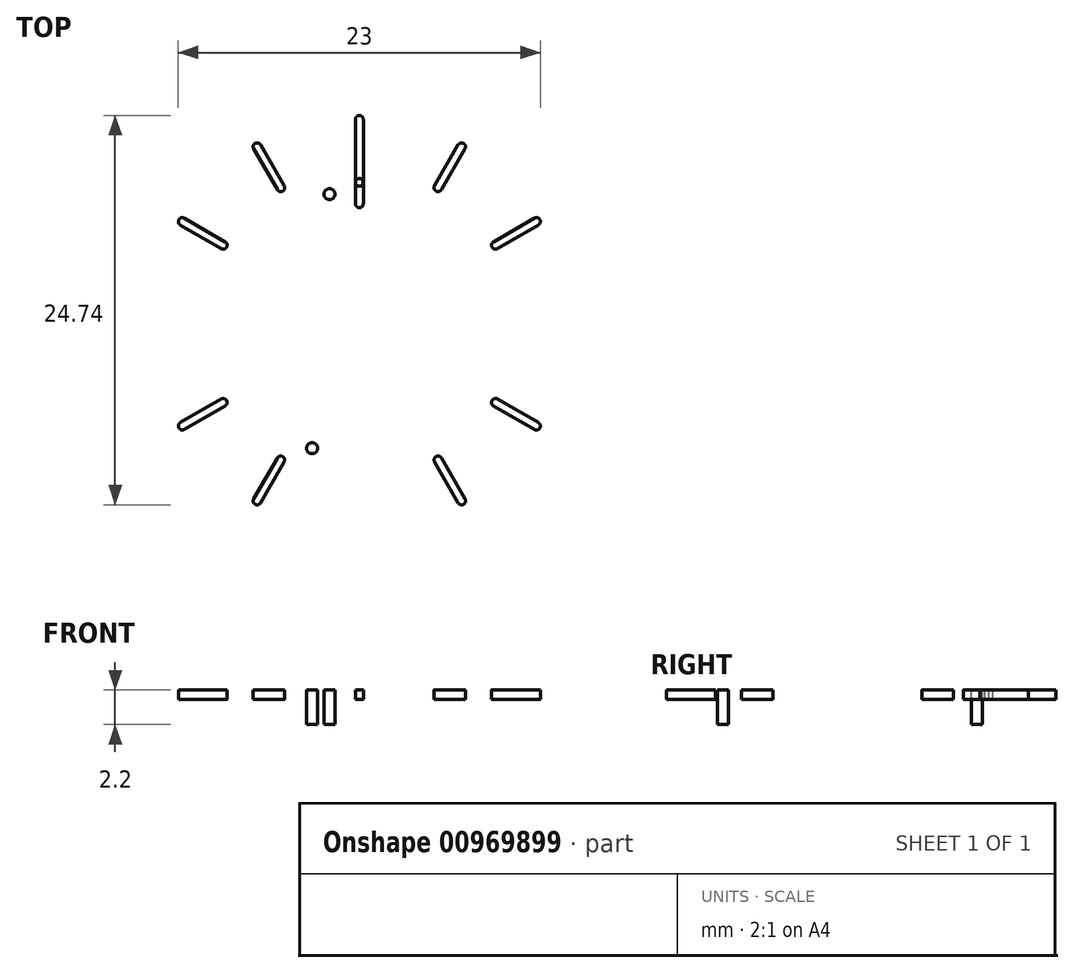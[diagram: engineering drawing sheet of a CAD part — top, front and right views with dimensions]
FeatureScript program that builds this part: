
annotation { "Feature Type Name" : "Feature", "Feature Type Description" : "" }
export const myFeature = defineFeature(function(context is Context, id is Id, definition is map)
    precondition{}
    {
        {
            var Q0;
            Q0=qCreatedBy(makeId("Top.planeOp"),FACE);
            var sketch = newSketch(context, id + "F0", { "sketchPlane" : qUnion([Q0])});
            skCircle(sketch, "E0", {"center": v(0, 0) * mm, "radius": 13.38 * mm});
            skLineSegment(sketch, "E1", {"start": v(0, -5.55) * mm, "end": v(0, 0) * mm, "construction": true});
            skLineSegment(sketch, "E2", {"start": v(-1.74, -5.55) * mm, "end": v(-4.94, -5.55) * mm, "construction": true});
            skLineSegment(sketch, "E3", {"start": v(0, -5.55) * mm, "end": v(3.2, -5.55) * mm, "construction": true});
            skLineSegment(sketch, "E4", {"start": v(-2.74, -5.55) * mm, "end": v(-2.74, -3.05) * mm, "construction": true});
            skLineSegment(sketch, "E5", {"start": v(3.2, -3.05) * mm, "end": v(3.2, -5.55) * mm, "construction": true});
            skLineSegment(sketch, "E6", {"start": v(-4.94, -3.15) * mm, "end": v(-2.81, -3.15) * mm, "construction": true});
            skLineSegment(sketch, "E7", {"start": v(-2.35, -3.15) * mm, "end": v(-2.35, -5.55) * mm, "construction": true});
            skLineSegment(sketch, "E8", {"start": v(-2.35, -5.55) * mm, "end": v(-0.22, -5.55) * mm, "construction": true});
            skArc(sketch, "E9.0.startCap", {"start": v(-3.03, -5.43) * mm, "mid": v(-3.22, -5.52) * mm, "end": v(-3.32, -5.33) * mm});
            skArc(sketch, "E9.0.endCap", {"start": v(-2.6, -3.14) * mm, "mid": v(-2.47, -3.04) * mm, "end": v(-2.33, -3.13) * mm});
            skLineSegment(sketch, "E9.0.left", {"start": v(-3.32, -5.33) * mm, "end": v(-2.6, -3.14) * mm});
            skLineSegment(sketch, "E9.0.right", {"start": v(-3.03, -5.43) * mm, "end": v(-2.46, -3.64) * mm});
            skArc(sketch, "E9.1.startCap", {"start": v(-2.6, -3.14) * mm, "mid": v(-2.47, -3.04) * mm, "end": v(-2.33, -3.13) * mm});
            skArc(sketch, "E9.1.endCap", {"start": v(-1.5, -5.33) * mm, "mid": v(-1.59, -5.52) * mm, "end": v(-1.78, -5.43) * mm});
            skLineSegment(sketch, "E9.1.left", {"start": v(-2.33, -3.13) * mm, "end": v(-1.5, -5.33) * mm});
            skLineSegment(sketch, "E9.1.right", {"start": v(-2.46, -3.64) * mm, "end": v(-1.78, -5.43) * mm});
            skLineSegment(sketch, "E10", {"start": v(-0.59, -3.05) * mm, "end": v(-0.59, -5.55) * mm, "construction": true});
            skArc(sketch, "E11.0.startCap", {"start": v(-1.5, -5.41) * mm, "mid": v(-1.68, -5.51) * mm, "end": v(-1.78, -5.33) * mm});
            skArc(sketch, "E11.0.endCap", {"start": v(-1.14, -3.16) * mm, "mid": v(-1, -3.05) * mm, "end": v(-0.86, -3.15) * mm});
            skLineSegment(sketch, "E11.0.left", {"start": v(-1.78, -5.33) * mm, "end": v(-1.14, -3.16) * mm});
            skLineSegment(sketch, "E11.0.right", {"start": v(-1.5, -5.41) * mm, "end": v(-0.97, -3.66) * mm});
            skArc(sketch, "E11.1.startCap", {"start": v(-1.14, -3.16) * mm, "mid": v(-1, -3.05) * mm, "end": v(-0.86, -3.15) * mm});
            skArc(sketch, "E11.1.endCap", {"start": v(0.02, -5.31) * mm, "mid": v(-0.06, -5.5) * mm, "end": v(-0.26, -5.43) * mm});
            skLineSegment(sketch, "E11.1.left", {"start": v(-0.86, -3.15) * mm, "end": v(0.02, -5.31) * mm});
            skLineSegment(sketch, "E11.1.right", {"start": v(-0.97, -3.66) * mm, "end": v(-0.26, -5.43) * mm});
            skLineSegment(sketch, "E12", {"start": v(1.33, -5.36) * mm, "end": v(1.33, -4.43) * mm});
            skLineSegment(sketch, "E13", {"start": v(1.33, -5.36) * mm, "end": v(1.63, -5.36) * mm});
            skLineSegment(sketch, "E14", {"start": v(1.63, -5.36) * mm, "end": v(1.63, -4.43) * mm});
            skLineSegment(sketch, "E15", {"start": v(1.63, -4.43) * mm, "end": v(2.48, -4.07) * mm});
            skLineSegment(sketch, "E16", {"start": v(1.33, -4.43) * mm, "end": v(1.33, -4.25) * mm});
            skLineSegment(sketch, "E17", {"start": v(1.33, -4.25) * mm, "end": v(2.36, -3.8) * mm});
            skLineSegment(sketch, "E18", {"start": v(2.36, -3.8) * mm, "end": v(1.33, -3.37) * mm});
            skLineSegment(sketch, "E19", {"start": v(1.63, -3.15) * mm, "end": v(2.61, -3.56) * mm});
            skLineSegment(sketch, "E20", {"start": v(2.48, -4.07) * mm, "end": v(2.61, -4.01) * mm});
            skArc(sketch, "E21", {"start": v(1.33, -5.36) * mm, "mid": v(1.48, -5.51) * mm, "end": v(1.63, -5.36) * mm});
            skArc(sketch, "E22", {"start": v(1.45, -3.07) * mm, "mid": v(1.3, -3.19) * mm, "end": v(1.33, -3.37) * mm});
            skArc(sketch, "E23", {"start": v(2.61, -4.01) * mm, "mid": v(2.72, -3.79) * mm, "end": v(2.61, -3.56) * mm});
            skPoint(sketch, "E24.orphan", {"position": v(2.48, -3.5) * mm});
            skLineSegment(sketch, "E25", {"start": v(1.63, -3.15) * mm, "end": v(1.45, -3.07) * mm});
            skPoint(sketch, "E26.end.orphan", {"position": v(1.33, -3.15) * mm});
            skSolve(sketch);
        }
        {
            var Q0;
            Q0=makeQuery(id+"F0.imprint","IMPRINT",FACE,{"disambiguationData":[TD([[makeQuery(id+"F0.imprint","IMPRINT",EDGE,{"derivedFrom":sQuery(id+"F0.wireOp",EDGE,"E0")}),1.0]])]});
            extrude(context, id + "F1", {"entities" : qUnion([Q0]), "depth" : .6 * mm});
        }
        {
            var Q0;
            Q0=makeQuery(id+"F1.opExtrude","CAP_FACE",FACE,{"disambiguationData":[OSD([sQuery(id+"F0.wireOp",EDGE,"E0"),sQuery(id+"F0.wireOp",EDGE,"81bd0466-aa7e-4cc1-a586-6c7cb0b4c62f.0.endCap"),sQuery(id+"F0.wireOp",EDGE,"81bd0466-aa7e-4cc1-a586-6c7cb0b4c62f.0.left"),sQuery(id+"F0.wireOp",EDGE,"81bd0466-aa7e-4cc1-a586-6c7cb0b4c62f.0.right"),sQuery(id+"F0.wireOp",EDGE,"81bd0466-aa7e-4cc1-a586-6c7cb0b4c62f.1.startCap"),sQuery(id+"F0.wireOp",EDGE,"81bd0466-aa7e-4cc1-a586-6c7cb0b4c62f.1.endCap"),sQuery(id+"F0.wireOp",EDGE,"81bd0466-aa7e-4cc1-a586-6c7cb0b4c62f.1.left"),sQuery(id+"F0.wireOp",EDGE,"81bd0466-aa7e-4cc1-a586-6c7cb0b4c62f.1.right"),sQuery(id+"F0.wireOp",EDGE,"fb5c5668-780e-4590-b6ff-0544ae9edb93.0.startCap"),sQuery(id+"F0.wireOp",EDGE,"fb5c5668-780e-4590-b6ff-0544ae9edb93.0.left"),sQuery(id+"F0.wireOp",EDGE,"fb5c5668-780e-4590-b6ff-0544ae9edb93.0.right"),sQuery(id+"F0.wireOp",EDGE,"fb5c5668-780e-4590-b6ff-0544ae9edb93.1.startCap"),sQuery(id+"F0.wireOp",EDGE,"fb5c5668-780e-4590-b6ff-0544ae9edb93.1.endCap"),sQuery(id+"F0.wireOp",EDGE,"fb5c5668-780e-4590-b6ff-0544ae9edb93.1.left"),sQuery(id+"F0.wireOp",EDGE,"fb5c5668-780e-4590-b6ff-0544ae9edb93.1.right"),sQuery(id+"F0.wireOp",EDGE,"44c2ab98-86a5-4347-a2b7-3f4ff268cd36.0.startCap"),sQuery(id+"F0.wireOp",EDGE,"44c2ab98-86a5-4347-a2b7-3f4ff268cd36.0.left"),sQuery(id+"F0.wireOp",EDGE,"44c2ab98-86a5-4347-a2b7-3f4ff268cd36.0.right"),sQuery(id+"F0.wireOp",EDGE,"44c2ab98-86a5-4347-a2b7-3f4ff268cd36.1.startCap"),sQuery(id+"F0.wireOp",EDGE,"44c2ab98-86a5-4347-a2b7-3f4ff268cd36.1.right"),sQuery(id+"F0.wireOp",EDGE,"44c2ab98-86a5-4347-a2b7-3f4ff268cd36.2.startCap"),sQuery(id+"F0.wireOp",EDGE,"44c2ab98-86a5-4347-a2b7-3f4ff268cd36.2.endCap"),sQuery(id+"F0.wireOp",EDGE,"44c2ab98-86a5-4347-a2b7-3f4ff268cd36.2.left"),sQuery(id+"F0.wireOp",EDGE,"d18c6785-b516-4534-9f84-c989dde87bb4.trimOffspring"),sQuery(id+"F0.wireOp",EDGE,"1f60e2fe-ff87-446b-ac51-922b63681436.trimOffspring")])],"isStart":false});
            var sketch = newSketch(context, id + "F2", { "sketchPlane" : qUnion([Q0])});
            skLineSegment(sketch, "E27", {"start": v(0, 12.99) * mm, "end": v(0, 8.99) * mm});
            skArc(sketch, "E28.0.startCap", {"start": v(-0.25, 12.99) * mm, "mid": v(0, 13.24) * mm, "end": v(0.25, 12.99) * mm});
            skArc(sketch, "E28.0.endCap", {"start": v(0.25, 8.99) * mm, "mid": v(0, 8.74) * mm, "end": v(-0.25, 8.99) * mm});
            skLineSegment(sketch, "E28.0.left", {"start": v(0.25, 12.99) * mm, "end": v(0.25, 8.99) * mm});
            skLineSegment(sketch, "E28.0.right", {"start": v(-0.25, 12.99) * mm, "end": v(-0.25, 8.99) * mm});
            skLineSegment(sketch, "E29.1.0", {"start": v(-12.99, 0.25) * mm, "end": v(-8.99, 0.25) * mm});
            skLineSegment(sketch, "E29.1.1", {"start": v(-12.99, -0.25) * mm, "end": v(-8.99, -0.25) * mm});
            skArc(sketch, "E29.1.2", {"start": v(-12.99, -0.25) * mm, "mid": v(-13.24, 0) * mm, "end": v(-12.99, 0.25) * mm});
            skArc(sketch, "E29.1.3", {"start": v(-8.99, 0.25) * mm, "mid": v(-8.74, 0) * mm, "end": v(-8.99, -0.25) * mm});
            skLineSegment(sketch, "E29.2.0", {"start": v(-0.25, -12.99) * mm, "end": v(-0.25, -8.99) * mm});
            skLineSegment(sketch, "E29.2.1", {"start": v(0.25, -12.99) * mm, "end": v(0.25, -8.99) * mm});
            skArc(sketch, "E29.2.2", {"start": v(0.25, -12.99) * mm, "mid": v(0, -13.24) * mm, "end": v(-0.25, -12.99) * mm});
            skArc(sketch, "E29.2.3", {"start": v(-0.25, -8.99) * mm, "mid": v(0, -8.74) * mm, "end": v(0.25, -8.99) * mm});
            skLineSegment(sketch, "E29.3.0", {"start": v(12.99, -0.25) * mm, "end": v(8.99, -0.25) * mm});
            skLineSegment(sketch, "E29.3.1", {"start": v(12.99, 0.25) * mm, "end": v(8.99, 0.25) * mm});
            skArc(sketch, "E29.3.2", {"start": v(12.99, 0.25) * mm, "mid": v(13.24, 0) * mm, "end": v(12.99, -0.25) * mm});
            skArc(sketch, "E29.3.3", {"start": v(8.99, -0.25) * mm, "mid": v(8.74, 0) * mm, "end": v(8.99, 0.25) * mm});
            skPoint(sketch, "E29.center", {"position": v(0, 0) * mm});
            skLineSegment(sketch, "E30.1.0", {"start": v(6.5, -11.25) * mm, "end": v(5, -8.65) * mm});
            skLineSegment(sketch, "E30.2.0", {"start": v(11.25, -6.5) * mm, "end": v(8.65, -5) * mm});
            skLineSegment(sketch, "E30.4.0", {"start": v(11.25, 6.5) * mm, "end": v(8.65, 5) * mm});
            skLineSegment(sketch, "E30.5.0", {"start": v(6.5, 11.25) * mm, "end": v(5, 8.65) * mm});
            skLineSegment(sketch, "E30.7.0", {"start": v(-6.5, 11.25) * mm, "end": v(-5, 8.65) * mm});
            skLineSegment(sketch, "E30.8.0", {"start": v(-11.25, 6.5) * mm, "end": v(-8.65, 5) * mm});
            skLineSegment(sketch, "E30.10.0", {"start": v(-11.25, -6.5) * mm, "end": v(-8.65, -5) * mm});
            skLineSegment(sketch, "E30.11.0", {"start": v(-6.5, -11.25) * mm, "end": v(-5, -8.65) * mm});
            skArc(sketch, "E31.0.startCap", {"start": v(-11.37, 6.28) * mm, "mid": v(-11.46, 6.62) * mm, "end": v(-11.12, 6.7) * mm});
            skArc(sketch, "E31.0.endCap", {"start": v(-8.52, 5.2) * mm, "mid": v(-8.43, 4.87) * mm, "end": v(-8.77, 4.78) * mm});
            skLineSegment(sketch, "E31.0.left", {"start": v(-11.12, 6.7) * mm, "end": v(-8.52, 5.2) * mm});
            skLineSegment(sketch, "E31.0.right", {"start": v(-11.37, 6.28) * mm, "end": v(-8.77, 4.78) * mm});
            skArc(sketch, "E31.1.startCap", {"start": v(-6.7, 11.12) * mm, "mid": v(-6.62, 11.46) * mm, "end": v(-6.28, 11.37) * mm});
            skArc(sketch, "E31.1.endCap", {"start": v(-4.78, 8.77) * mm, "mid": v(-4.87, 8.43) * mm, "end": v(-5.2, 8.52) * mm});
            skLineSegment(sketch, "E31.1.left", {"start": v(-6.28, 11.37) * mm, "end": v(-4.78, 8.77) * mm});
            skLineSegment(sketch, "E31.1.right", {"start": v(-6.7, 11.12) * mm, "end": v(-5.2, 8.52) * mm});
            skArc(sketch, "E31.2.startCap", {"start": v(6.28, 11.37) * mm, "mid": v(6.62, 11.46) * mm, "end": v(6.7, 11.12) * mm});
            skArc(sketch, "E31.2.endCap", {"start": v(5.2, 8.52) * mm, "mid": v(4.87, 8.43) * mm, "end": v(4.78, 8.77) * mm});
            skLineSegment(sketch, "E31.2.left", {"start": v(6.7, 11.12) * mm, "end": v(5.2, 8.52) * mm});
            skLineSegment(sketch, "E31.2.right", {"start": v(6.28, 11.37) * mm, "end": v(4.78, 8.77) * mm});
            skArc(sketch, "E31.3.startCap", {"start": v(11.12, 6.7) * mm, "mid": v(11.46, 6.62) * mm, "end": v(11.37, 6.28) * mm});
            skArc(sketch, "E31.3.endCap", {"start": v(8.77, 4.78) * mm, "mid": v(8.43, 4.87) * mm, "end": v(8.52, 5.2) * mm});
            skLineSegment(sketch, "E31.3.left", {"start": v(11.37, 6.28) * mm, "end": v(8.77, 4.78) * mm});
            skLineSegment(sketch, "E31.3.right", {"start": v(11.12, 6.7) * mm, "end": v(8.52, 5.2) * mm});
            skArc(sketch, "E31.4.startCap", {"start": v(11.37, -6.28) * mm, "mid": v(11.46, -6.62) * mm, "end": v(11.12, -6.7) * mm});
            skArc(sketch, "E31.4.endCap", {"start": v(8.52, -5.2) * mm, "mid": v(8.43, -4.87) * mm, "end": v(8.77, -4.78) * mm});
            skLineSegment(sketch, "E31.4.left", {"start": v(11.12, -6.7) * mm, "end": v(8.52, -5.2) * mm});
            skLineSegment(sketch, "E31.4.right", {"start": v(11.37, -6.28) * mm, "end": v(8.77, -4.78) * mm});
            skArc(sketch, "E31.5.startCap", {"start": v(6.7, -11.12) * mm, "mid": v(6.62, -11.46) * mm, "end": v(6.28, -11.37) * mm});
            skArc(sketch, "E31.5.endCap", {"start": v(4.78, -8.77) * mm, "mid": v(4.87, -8.43) * mm, "end": v(5.2, -8.52) * mm});
            skLineSegment(sketch, "E31.5.left", {"start": v(6.28, -11.37) * mm, "end": v(4.78, -8.77) * mm});
            skLineSegment(sketch, "E31.5.right", {"start": v(6.7, -11.12) * mm, "end": v(5.2, -8.52) * mm});
            skArc(sketch, "E31.6.startCap", {"start": v(-6.28, -11.37) * mm, "mid": v(-6.62, -11.46) * mm, "end": v(-6.7, -11.12) * mm});
            skArc(sketch, "E31.6.endCap", {"start": v(-5.2, -8.52) * mm, "mid": v(-4.87, -8.43) * mm, "end": v(-4.78, -8.77) * mm});
            skLineSegment(sketch, "E31.6.left", {"start": v(-6.7, -11.12) * mm, "end": v(-5.2, -8.52) * mm});
            skLineSegment(sketch, "E31.6.right", {"start": v(-6.28, -11.37) * mm, "end": v(-4.78, -8.77) * mm});
            skArc(sketch, "E31.7.startCap", {"start": v(-11.12, -6.7) * mm, "mid": v(-11.46, -6.62) * mm, "end": v(-11.37, -6.28) * mm});
            skArc(sketch, "E31.7.endCap", {"start": v(-8.77, -4.78) * mm, "mid": v(-8.43, -4.87) * mm, "end": v(-8.52, -5.2) * mm});
            skLineSegment(sketch, "E31.7.left", {"start": v(-11.37, -6.28) * mm, "end": v(-8.77, -4.78) * mm});
            skLineSegment(sketch, "E31.7.right", {"start": v(-11.12, -6.7) * mm, "end": v(-8.52, -5.2) * mm});
            skCircle(sketch, "E32", {"center": v(0, 0) * mm, "radius": 0.75 * mm});
            skLineSegment(sketch, "E33", {"start": v(0, 8.99) * mm, "end": v(0, 7.63) * mm});
            skPoint(sketch, "E33.endSnap0", {"position": v(0, 8.74) * mm});
            skArc(sketch, "E34.0.startCap", {"start": v(-0.25, 8.99) * mm, "mid": v(0, 9.24) * mm, "end": v(0.25, 8.99) * mm});
            skArc(sketch, "E34.0.endCap", {"start": v(0.25, 7.63) * mm, "mid": v(0, 7.38) * mm, "end": v(-0.25, 7.63) * mm});
            skLineSegment(sketch, "E34.0.left", {"start": v(0.25, 8.99) * mm, "end": v(0.25, 7.63) * mm});
            skLineSegment(sketch, "E34.0.right", {"start": v(-0.25, 8.99) * mm, "end": v(-0.25, 7.63) * mm});
            skSolve(sketch);
        }
        {
            var Q0;
            Q0=makeQuery(id+"F2.imprint","IMPRINT",FACE,{"disambiguationData":[TD([[makeQuery(id+"F2.imprint","IMPRINT",EDGE,{"derivedFrom":sQuery(id+"F2.wireOp",EDGE,"E31.0.startCap")}),-1.0]])]});
            var Q1;
            Q1=makeQuery(id+"F2.imprint","IMPRINT",FACE,{"disambiguationData":[TD([[makeQuery(id+"F2.imprint","IMPRINT",EDGE,{"derivedFrom":sQuery(id+"F2.wireOp",EDGE,"E29.1.0")}),-1.0]])]});
            var Q2;
            Q2=makeQuery(id+"F2.imprint","IMPRINT",FACE,{"disambiguationData":[TD([[makeQuery(id+"F2.imprint","IMPRINT",EDGE,{"derivedFrom":sQuery(id+"F2.wireOp",EDGE,"E31.1.startCap")}),-1.0]])]});
            var Q3;
            Q3=makeQuery(id+"F2.imprint","IMPRINT",FACE,{"disambiguationData":[TD([[makeQuery(id+"F2.imprint","IMPRINT",EDGE,{"derivedFrom":sQuery(id+"F2.wireOp",EDGE,"E28.0.startCap")}),-1.0]])]});
            var Q4;
            Q4=makeQuery(id+"F2.imprint","IMPRINT",FACE,{"disambiguationData":[TD([[makeQuery(id+"F2.imprint","IMPRINT",EDGE,{"derivedFrom":sQuery(id+"F2.wireOp",EDGE,"E31.2.startCap")}),-1.0]])]});
            var Q5;
            Q5=makeQuery(id+"F2.imprint","IMPRINT",FACE,{"disambiguationData":[TD([[makeQuery(id+"F2.imprint","IMPRINT",EDGE,{"derivedFrom":sQuery(id+"F2.wireOp",EDGE,"E31.3.startCap")}),-1.0]])]});
            var Q6;
            Q6=makeQuery(id+"F2.imprint","IMPRINT",FACE,{"disambiguationData":[TD([[makeQuery(id+"F2.imprint","IMPRINT",EDGE,{"derivedFrom":sQuery(id+"F2.wireOp",EDGE,"E29.3.0")}),-1.0]])]});
            var Q7;
            Q7=makeQuery(id+"F2.imprint","IMPRINT",FACE,{"disambiguationData":[TD([[makeQuery(id+"F2.imprint","IMPRINT",EDGE,{"derivedFrom":sQuery(id+"F2.wireOp",EDGE,"E31.4.startCap")}),-1.0]])]});
            var Q8;
            Q8=makeQuery(id+"F2.imprint","IMPRINT",FACE,{"disambiguationData":[TD([[makeQuery(id+"F2.imprint","IMPRINT",EDGE,{"derivedFrom":sQuery(id+"F2.wireOp",EDGE,"E29.2.0")}),-1.0]])]});
            var Q9;
            Q9=makeQuery(id+"F2.imprint","IMPRINT",FACE,{"disambiguationData":[TD([[makeQuery(id+"F2.imprint","IMPRINT",EDGE,{"derivedFrom":sQuery(id+"F2.wireOp",EDGE,"E31.5.startCap")}),-1.0]])]});
            var Q10;
            Q10=makeQuery(id+"F2.imprint","IMPRINT",FACE,{"disambiguationData":[TD([[makeQuery(id+"F2.imprint","IMPRINT",EDGE,{"derivedFrom":sQuery(id+"F2.wireOp",EDGE,"E31.6.startCap")}),-1.0]])]});
            var Q11;
            Q11=makeQuery(id+"F2.imprint","IMPRINT",FACE,{"disambiguationData":[TD([[makeQuery(id+"F2.imprint","IMPRINT",EDGE,{"derivedFrom":sQuery(id+"F2.wireOp",EDGE,"E31.7.startCap")}),-1.0]])]});
            var Q12;
            Q12=makeQuery(id+"F2.imprint","IMPRINT",FACE,{"disambiguationData":[TD([[makeQuery(id+"F2.imprint","IMPRINT",EDGE,{"derivedFrom":sQuery(id+"F2.wireOp",EDGE,"E32")}),1.0]])]});
            var Q13;
            Q13=makeQuery(id+"F2.imprint","IMPRINT",FACE,{"disambiguationData":[TD([[makeQuery(id+"F2.imprint","IMPRINT",EDGE,{"derivedFrom":sQuery(id+"F2.wireOp",EDGE,"E34.0.endCap")}),-1.0]])]});
            var Q14;
            {var subQ0=sQuery(id+"F2.wireOp",EDGE,"E33");var subQ1=sQuery(id+"F2.wireOp",EDGE,"E27");var subQ2=makeQuery(id+"F2.imprint","INTERSECT",VERTEX,{"derivedFrom":[subQ1,subQ0]});Q14=makeQuery(id+"F2.imprint","IMPRINT",FACE,{"disambiguationData":[TD([[makeQuery(id+"F2.imprint","IMPRINT",EDGE,{"disambiguationData":[TD([[subQ2,1.0]])],"derivedFrom":subQ1}),-1.0]])]});}
            var Q15;
            {var subQ0=sQuery(id+"F2.wireOp",EDGE,"E33");var subQ1=sQuery(id+"F2.wireOp",EDGE,"E27");var subQ2=makeQuery(id+"F2.imprint","INTERSECT",VERTEX,{"derivedFrom":[subQ1,subQ0]});Q15=makeQuery(id+"F2.imprint","IMPRINT",FACE,{"disambiguationData":[TD([[makeQuery(id+"F2.imprint","IMPRINT",EDGE,{"disambiguationData":[TD([[subQ2,1.0]])],"derivedFrom":subQ1}),1.0]])]});}
            extrude(context, id + "F3", {"entities" : qUnion([Q0, Q1, Q2, Q3, Q4, Q5, Q6, Q7, Q8, Q9, Q10, Q11, Q12, Q13, Q14, Q15]), "operationType" : NewBodyOperationType.REMOVE, "endBound" : BoundingType.UP_TO_NEXT, "oppositeDirection" : true, "depth" : 25 * mm});
        }
        {
            var Q0;
            Q0=makeQuery(id+"F1.opExtrude","CAP_FACE",FACE,{"disambiguationData":[OSD([sQuery(id+"F0.wireOp",EDGE,"E0"),sQuery(id+"F0.wireOp",EDGE,"81bd0466-aa7e-4cc1-a586-6c7cb0b4c62f.0.endCap"),sQuery(id+"F0.wireOp",EDGE,"81bd0466-aa7e-4cc1-a586-6c7cb0b4c62f.0.left"),sQuery(id+"F0.wireOp",EDGE,"81bd0466-aa7e-4cc1-a586-6c7cb0b4c62f.0.right"),sQuery(id+"F0.wireOp",EDGE,"81bd0466-aa7e-4cc1-a586-6c7cb0b4c62f.1.startCap"),sQuery(id+"F0.wireOp",EDGE,"81bd0466-aa7e-4cc1-a586-6c7cb0b4c62f.1.endCap"),sQuery(id+"F0.wireOp",EDGE,"81bd0466-aa7e-4cc1-a586-6c7cb0b4c62f.1.left"),sQuery(id+"F0.wireOp",EDGE,"81bd0466-aa7e-4cc1-a586-6c7cb0b4c62f.1.right"),sQuery(id+"F0.wireOp",EDGE,"fb5c5668-780e-4590-b6ff-0544ae9edb93.0.startCap"),sQuery(id+"F0.wireOp",EDGE,"fb5c5668-780e-4590-b6ff-0544ae9edb93.0.left"),sQuery(id+"F0.wireOp",EDGE,"fb5c5668-780e-4590-b6ff-0544ae9edb93.0.right"),sQuery(id+"F0.wireOp",EDGE,"fb5c5668-780e-4590-b6ff-0544ae9edb93.1.startCap"),sQuery(id+"F0.wireOp",EDGE,"fb5c5668-780e-4590-b6ff-0544ae9edb93.1.endCap"),sQuery(id+"F0.wireOp",EDGE,"fb5c5668-780e-4590-b6ff-0544ae9edb93.1.left"),sQuery(id+"F0.wireOp",EDGE,"fb5c5668-780e-4590-b6ff-0544ae9edb93.1.right"),sQuery(id+"F0.wireOp",EDGE,"44c2ab98-86a5-4347-a2b7-3f4ff268cd36.0.startCap"),sQuery(id+"F0.wireOp",EDGE,"44c2ab98-86a5-4347-a2b7-3f4ff268cd36.0.left"),sQuery(id+"F0.wireOp",EDGE,"44c2ab98-86a5-4347-a2b7-3f4ff268cd36.0.right"),sQuery(id+"F0.wireOp",EDGE,"44c2ab98-86a5-4347-a2b7-3f4ff268cd36.1.startCap"),sQuery(id+"F0.wireOp",EDGE,"44c2ab98-86a5-4347-a2b7-3f4ff268cd36.1.right"),sQuery(id+"F0.wireOp",EDGE,"44c2ab98-86a5-4347-a2b7-3f4ff268cd36.2.startCap"),sQuery(id+"F0.wireOp",EDGE,"44c2ab98-86a5-4347-a2b7-3f4ff268cd36.2.endCap"),sQuery(id+"F0.wireOp",EDGE,"44c2ab98-86a5-4347-a2b7-3f4ff268cd36.2.left"),sQuery(id+"F0.wireOp",EDGE,"d18c6785-b516-4534-9f84-c989dde87bb4.trimOffspring"),sQuery(id+"F0.wireOp",EDGE,"1f60e2fe-ff87-446b-ac51-922b63681436.trimOffspring")])],"isStart":false});
            var sketch = newSketch(context, id + "F4", { "sketchPlane" : qUnion([Q0])});
            skLineSegment(sketch, "E35", {"start": v(0, 0) * mm, "end": v(0, -7.9) * mm, "construction": true});
            skLineSegment(sketch, "E36", {"start": v(0, -7.9) * mm, "end": v(-3, -7.9) * mm, "construction": true});
            skLineSegment(sketch, "E37", {"start": v(0, 0) * mm, "end": v(0, 8.23) * mm, "construction": true});
            skLineSegment(sketch, "E38", {"start": v(0, 8.23) * mm, "end": v(-1.9, 8.23) * mm, "construction": true});
            skCircle(sketch, "E39", {"center": v(-1.9, 8.23) * mm, "radius": 0.35 * mm});
            skCircle(sketch, "E40", {"center": v(-3, -7.9) * mm, "radius": 0.35 * mm});
            skSolve(sketch);
        }
        {
            var Q0;
            Q0=qSketchRegion(id+"F4",true);
            extrude(context, id + "F5", {"entities" : qUnion([Q0]), "operationType" : NewBodyOperationType.ADD, "oppositeDirection" : true, "depth" : 2.2 * mm});
        }
    });
